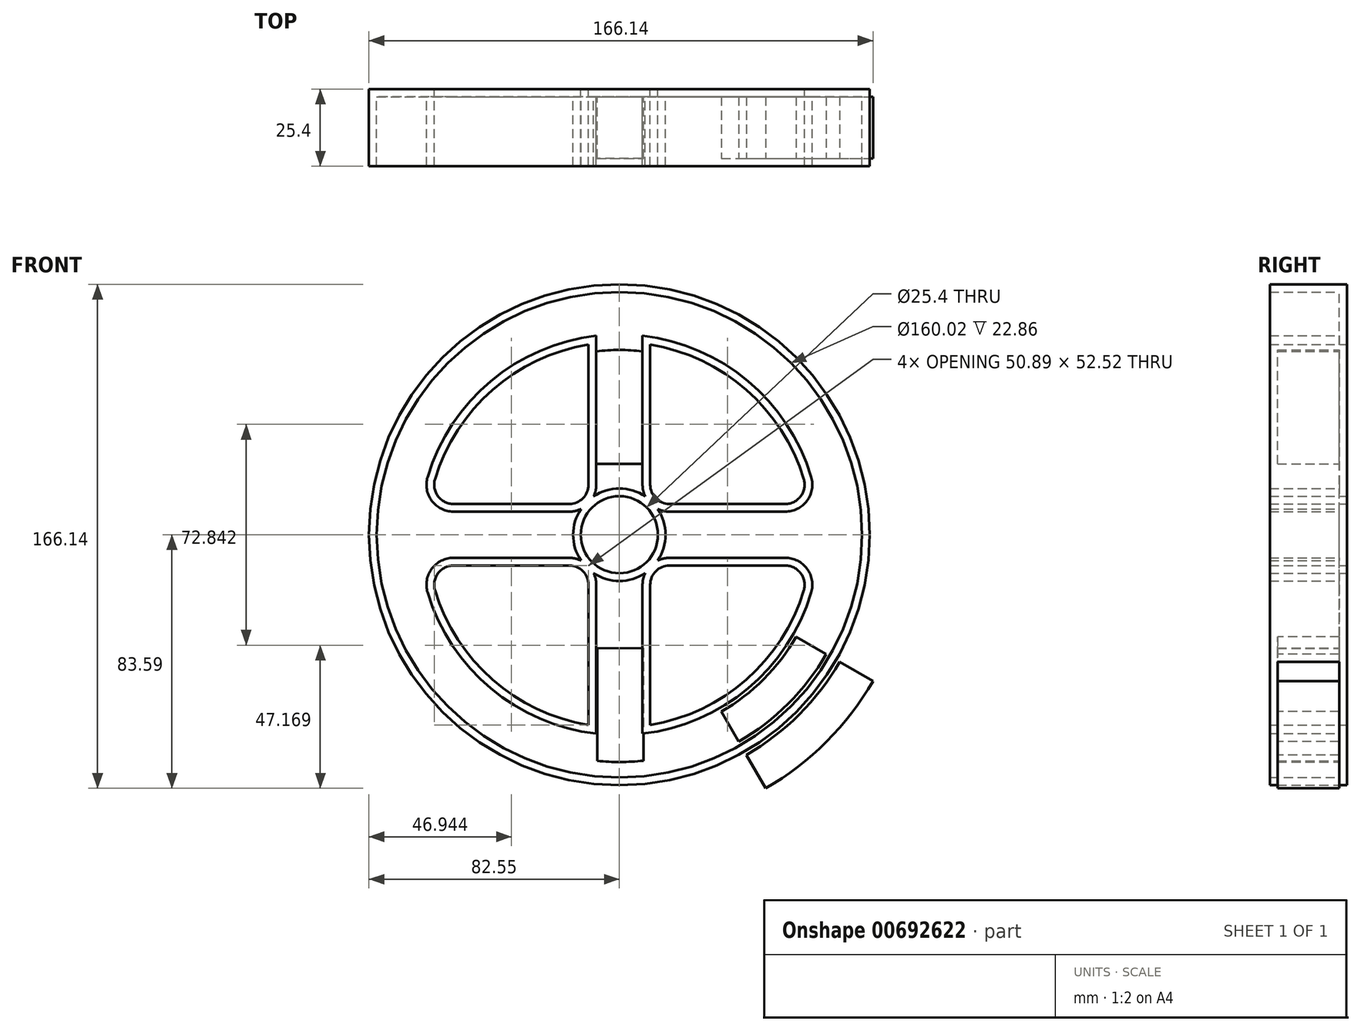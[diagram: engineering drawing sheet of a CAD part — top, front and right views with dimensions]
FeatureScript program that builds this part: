
annotation { "Feature Type Name" : "Feature", "Feature Type Description" : "" }
export const myFeature = defineFeature(function(context is Context, id is Id, definition is map)
    precondition{}
    {
        {
            var Q0;
            Q0=qCreatedBy(makeId("Front.planeOp"),FACE);
            var sketch = newSketch(context, id + "F0", { "sketchPlane" : qUnion([Q0])});
            skCircle(sketch, "E0", {"center": v(0, 0) * mm, "radius": 82.55 * mm});
            skArc(sketch, "E1", {"start": v(-10.16, 62.68) * mm, "mid": v(-41.83, 47.77) * mm, "end": v(-60.8, 18.34) * mm});
            skLineSegment(sketch, "E2", {"start": v(10.16, 62.68) * mm, "end": v(10.16, 16.51) * mm});
            skLineSegment(sketch, "E3", {"start": v(-10.16, 62.68) * mm, "end": v(-10.16, 16.51) * mm});
            skLineSegment(sketch, "E4", {"start": v(-54.71, 10.16) * mm, "end": v(-16.5, 10.16) * mm});
            skLineSegment(sketch, "E5", {"start": v(-54.71, -10.16) * mm, "end": v(-16.5, -10.16) * mm});
            skLineSegment(sketch, "E6.trimOffspring", {"start": v(16.51, 10.16) * mm, "end": v(54.71, 10.16) * mm});
            skLineSegment(sketch, "E7.trimOffspring", {"start": v(10.16, -16.51) * mm, "end": v(10.16, -62.68) * mm});
            skLineSegment(sketch, "E8.trimOffspring", {"start": v(16.51, -10.16) * mm, "end": v(54.71, -10.16) * mm});
            skLineSegment(sketch, "E9.trimOffspring", {"start": v(-10.16, -16.51) * mm, "end": v(-10.16, -62.68) * mm});
            skArc(sketch, "E10.trimOffspring", {"start": v(-60.8, -18.34) * mm, "mid": v(-41.83, -47.77) * mm, "end": v(-10.16, -62.68) * mm});
            skArc(sketch, "E11.trimOffspring", {"start": v(10.16, -62.68) * mm, "mid": v(41.83, -47.77) * mm, "end": v(60.8, -18.34) * mm});
            skArc(sketch, "E12.trimOffspring", {"start": v(60.8, 18.34) * mm, "mid": v(41.83, 47.77) * mm, "end": v(10.16, 62.68) * mm});
            skPoint(sketch, "E13.visualSharp", {"position": v(-10.16, 10.16) * mm});
            skArc(sketch, "E13.filletArc", {"start": v(-16.5, 10.16) * mm, "mid": v(-12.02, 12.02) * mm, "end": v(-10.16, 16.51) * mm});
            skPoint(sketch, "E14.visualSharp", {"position": v(10.16, 10.16) * mm});
            skArc(sketch, "E14.filletArc", {"start": v(10.16, 16.51) * mm, "mid": v(12.02, 12.02) * mm, "end": v(16.51, 10.16) * mm});
            skPoint(sketch, "E15.visualSharp", {"position": v(10.16, -10.16) * mm});
            skArc(sketch, "E15.filletArc", {"start": v(16.51, -10.16) * mm, "mid": v(12.02, -12.02) * mm, "end": v(10.16, -16.51) * mm});
            skPoint(sketch, "E16.visualSharp", {"position": v(-10.16, -10.16) * mm});
            skArc(sketch, "E16.filletArc", {"start": v(-10.16, -16.51) * mm, "mid": v(-12.02, -12.02) * mm, "end": v(-16.5, -10.16) * mm});
            skCircle(sketch, "E17", {"center": v(0, 0) * mm, "radius": 12.7 * mm});
            skPoint(sketch, "E18.visualSharp", {"position": v(-62.68, 10.16) * mm});
            skArc(sketch, "E18.filletArc", {"start": v(-60.8, 18.34) * mm, "mid": v(-59.81, 12.72) * mm, "end": v(-54.71, 10.16) * mm});
            skPoint(sketch, "E19.visualSharp", {"position": v(-62.68, -10.16) * mm});
            skArc(sketch, "E19.filletArc", {"start": v(-54.71, -10.16) * mm, "mid": v(-59.81, -12.72) * mm, "end": v(-60.8, -18.34) * mm});
            skPoint(sketch, "E20.visualSharp", {"position": v(62.68, -10.16) * mm});
            skArc(sketch, "E20.filletArc", {"start": v(60.8, -18.34) * mm, "mid": v(59.81, -12.72) * mm, "end": v(54.71, -10.16) * mm});
            skPoint(sketch, "E21.visualSharp", {"position": v(62.68, 10.16) * mm});
            skArc(sketch, "E21.filletArc", {"start": v(54.71, 10.16) * mm, "mid": v(59.81, 12.72) * mm, "end": v(60.8, 18.34) * mm});
            skCircle(sketch, "E22", {"center": v(0, 0) * mm, "radius": 5.4 * mm});
            skSolve(sketch);
        }
        {
            var Q0;
            Q0=qCreatedBy(makeId("Front.planeOp"),FACE);
            var sketch = newSketch(context, id + "F1", { "sketchPlane" : qUnion([Q0])});
            skArc(sketch, "E23", {"start": v(7.56, 60.45) * mm, "mid": v(-0.06, 60.92) * mm, "end": v(-7.68, 60.44) * mm});
            skLineSegment(sketch, "E24.bottom", {"start": v(-7.68, 23.31) * mm, "end": v(7.56, 23.31) * mm});
            skLineSegment(sketch, "E24.left", {"start": v(-7.68, 23.31) * mm, "end": v(-7.68, 60.44) * mm});
            skLineSegment(sketch, "E24.right", {"start": v(7.56, 23.31) * mm, "end": v(7.56, 60.45) * mm});
            skArc(sketch, "E25", {"start": v(-7.34, -74.57) * mm, "mid": v(0.28, -74.93) * mm, "end": v(7.9, -74.51) * mm});
            skLineSegment(sketch, "E26.bottom", {"start": v(-7.34, -37.43) * mm, "end": v(7.9, -37.38) * mm});
            skLineSegment(sketch, "E26.left", {"start": v(-7.34, -37.43) * mm, "end": v(-7.34, -74.57) * mm});
            skLineSegment(sketch, "E26.right", {"start": v(7.9, -37.38) * mm, "end": v(7.9, -74.51) * mm});
            skSolve(sketch);
        }
        {
            var Q0;
            Q0=makeQuery(id+"F1.imprint","IMPRINT",FACE,{"disambiguationData":[TD([[makeQuery(id+"F1.imprint","IMPRINT",EDGE,{"derivedFrom":sQuery(id+"F1.wireOp",EDGE,"E23")}),1.0]])]});
            extrude(context, id + "F2", {"entities" : qUnion([Q0]), "endBound" : BoundingType.SYMMETRIC, "depth" : 20.32 * mm, "offsetDistance" : 25.4 * mm});
        }
        {
            var Q0;
            Q0=sQuery(id+"F1.wireOp",EDGE,"E26.left");
            var Q1;
            Q1=sQuery(id+"F1.wireOp",EDGE,"E26.bottom");
            var Q2;
            Q2=sQuery(id+"F1.wireOp",EDGE,"E26.right");
            var Q3;
            Q3=sQuery(id+"F1.wireOp",EDGE,"E25");
            extrude(context, id + "F3", {"bodyType" : ToolBodyType.SURFACE, "surfaceEntities" : qUnion([Q0, Q1, Q2, Q3]), "endBound" : BoundingType.SYMMETRIC, "depth" : 20.32 * mm, "offsetDistance" : 25.4 * mm});
        }
        {
            var Q0;
            Q0=qSketchRegion(id+"F1",true);
            extrude(context, id + "F4", {"entities" : qUnion([Q0]), "operationType" : NewBodyOperationType.ADD, "endBound" : BoundingType.SYMMETRIC, "depth" : 20.32 * mm, "offsetDistance" : 25.4 * mm});
        }
        {
            var Q0;
            Q0=qSketchRegion(id+"F0",true);
            extrude(context, id + "F5", {"entities" : qUnion([Q0]), "endBound" : BoundingType.SYMMETRIC, "depth" : 25.4 * mm, "offsetDistance" : 25.4 * mm});
        }
        {
            var Q0;
            Q0=makeQuery(id+"F5.opExtrude","CAP_FACE",FACE,{"disambiguationData":[OSD([sQuery(id+"F0.wireOp",EDGE,"E0"),sQuery(id+"F0.wireOp",EDGE,"E1"),sQuery(id+"F0.wireOp",EDGE,"E2"),sQuery(id+"F0.wireOp",EDGE,"E3"),sQuery(id+"F0.wireOp",EDGE,"E4"),sQuery(id+"F0.wireOp",EDGE,"E5"),sQuery(id+"F0.wireOp",EDGE,"E6.trimOffspring"),sQuery(id+"F0.wireOp",EDGE,"E7.trimOffspring"),sQuery(id+"F0.wireOp",EDGE,"E8.trimOffspring"),sQuery(id+"F0.wireOp",EDGE,"E9.trimOffspring"),sQuery(id+"F0.wireOp",EDGE,"E10.trimOffspring"),sQuery(id+"F0.wireOp",EDGE,"E11.trimOffspring"),sQuery(id+"F0.wireOp",EDGE,"E12.trimOffspring"),sQuery(id+"F0.wireOp",EDGE,"E13.filletArc"),sQuery(id+"F0.wireOp",EDGE,"E14.filletArc"),sQuery(id+"F0.wireOp",EDGE,"E15.filletArc"),sQuery(id+"F0.wireOp",EDGE,"E16.filletArc"),sQuery(id+"F0.wireOp",EDGE,"E17"),sQuery(id+"F0.wireOp",EDGE,"E18.filletArc"),sQuery(id+"F0.wireOp",EDGE,"E19.filletArc"),sQuery(id+"F0.wireOp",EDGE,"E20.filletArc"),sQuery(id+"F0.wireOp",EDGE,"E21.filletArc")])],"isStart":false});
            shell(context, id + "F6", {"entities" : qUnion([Q0]), "thickness" : 2.54 * mm});
        }
        {
            var Q0;
            Q0=qCreatedBy(makeId("Front.planeOp"),FACE);
            var sketch = newSketch(context, id + "F7", { "sketchPlane" : qUnion([Q0])});
            skLineSegment(sketch, "E27", {"start": v(58.3, -33.66) * mm, "end": v(68.2, -39.37) * mm});
            skLineSegment(sketch, "E28", {"start": v(33.65, -58.3) * mm, "end": v(39.37, -68.2) * mm});
            skArc(sketch, "E29", {"start": v(33.65, -58.3) * mm, "mid": v(47.6, -47.6) * mm, "end": v(58.3, -33.66) * mm});
            skArc(sketch, "E30", {"start": v(39.37, -68.2) * mm, "mid": v(55.68, -55.68) * mm, "end": v(68.2, -39.37) * mm});
            skArc(sketch, "E31", {"start": v(41.9, -72.6) * mm, "mid": v(59.27, -59.27) * mm, "end": v(72.6, -41.91) * mm});
            skArc(sketch, "E32", {"start": v(48.26, -83.59) * mm, "mid": v(68.25, -68.25) * mm, "end": v(83.59, -48.26) * mm});
            skLineSegment(sketch, "E33.trimOffspring", {"start": v(41.9, -72.6) * mm, "end": v(48.26, -83.59) * mm});
            skLineSegment(sketch, "E34.trimOffspring", {"start": v(72.6, -41.91) * mm, "end": v(83.59, -48.26) * mm});
            skLineSegment(sketch, "E35", {"start": v(0, 0) * mm, "end": v(113.59, 0) * mm, "construction": true});
            skSolve(sketch);
        }
        {
            var Q0;
            Q0=makeQuery(id+"F7.imprint","IMPRINT",FACE,{"disambiguationData":[TD([[makeQuery(id+"F7.imprint","IMPRINT",EDGE,{"derivedFrom":sQuery(id+"F7.wireOp",EDGE,"E27")}),-1.0]])]});
            var Q1;
            Q1=makeQuery(id+"F7.imprint","IMPRINT",FACE,{"disambiguationData":[TD([[makeQuery(id+"F7.imprint","IMPRINT",EDGE,{"derivedFrom":sQuery(id+"F7.wireOp",EDGE,"E31")}),-1.0]])]});
            extrude(context, id + "F8", {"entities" : qUnion([Q0, Q1]), "endBound" : BoundingType.SYMMETRIC, "oppositeDirection" : true, "depth" : 20.32 * mm, "offsetDistance" : 25.4 * mm});
        }
        {
            var Q0;
            Q0=makeQuery(id+"F0.imprint","IMPRINT",FACE,{"disambiguationData":[TD([[makeQuery(id+"F0.imprint","IMPRINT",EDGE,{"derivedFrom":sQuery(id+"F0.wireOp",EDGE,"E22")}),1.0]])]});
            extrude(context, id + "F9", {"entities" : qUnion([Q0]), "operationType" : NewBodyOperationType.REMOVE, "endBound" : BoundingType.SYMMETRIC, "oppositeDirection" : true, "depth" : 25.4 * mm, "offsetDistance" : 25.4 * mm});
        }
    });
